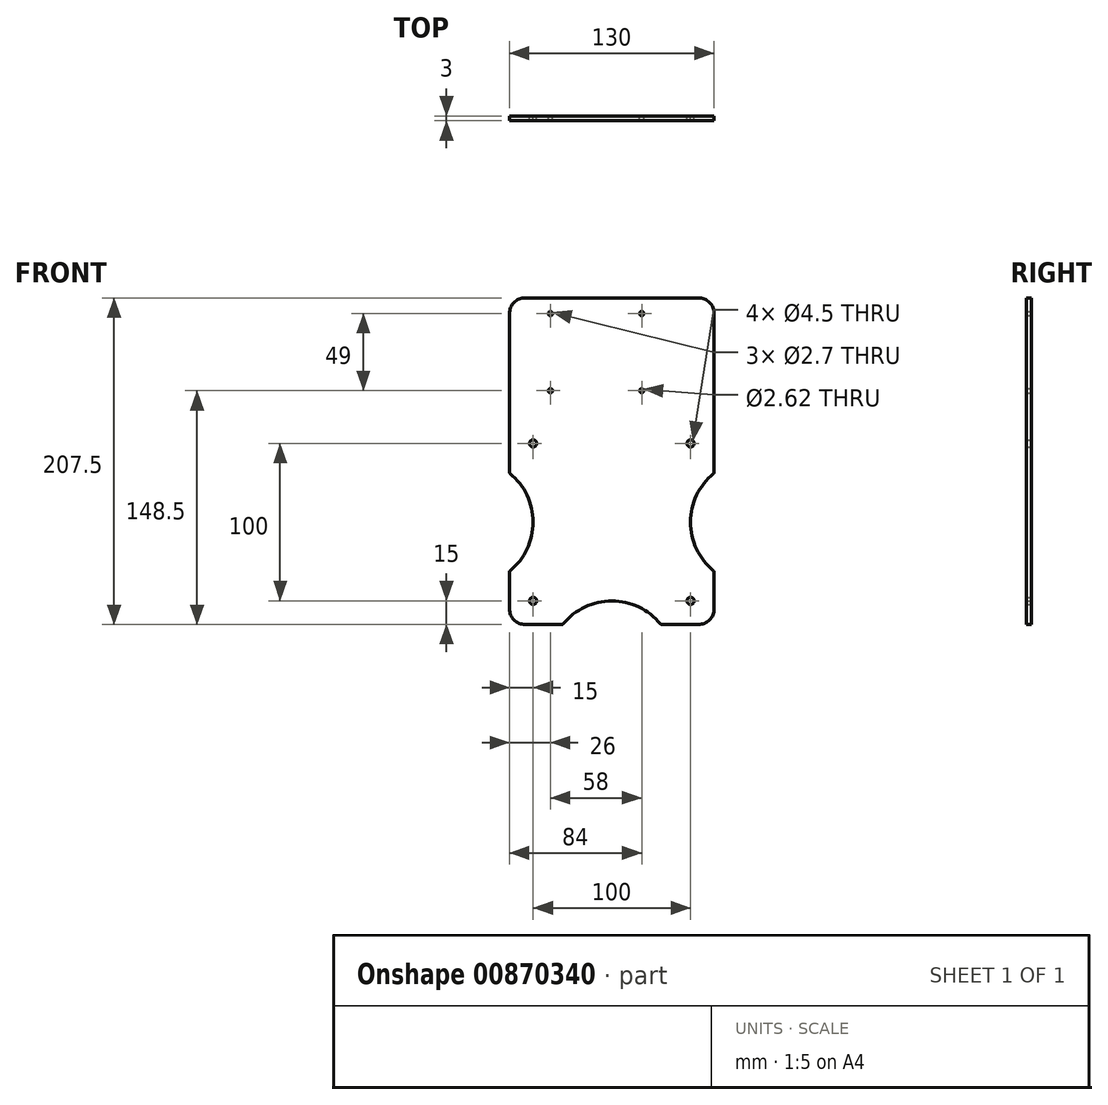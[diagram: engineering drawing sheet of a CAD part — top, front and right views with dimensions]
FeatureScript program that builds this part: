
annotation { "Feature Type Name" : "Feature", "Feature Type Description" : "" }
export const myFeature = defineFeature(function(context is Context, id is Id, definition is map)
    precondition{}
    {
        {
            var Q0;
            Q0=qCreatedBy(makeId("Front.planeOp"),FACE);
            var sketch = newSketch(context, id + "F0", { "sketchPlane" : qUnion([Q0])});
            skLineSegment(sketch, "E0.bottom", {"start": v(10, 0) * mm, "end": v(120, 0) * mm});
            skLineSegment(sketch, "E0.top", {"start": v(10, 207.5) * mm, "end": v(120, 207.5) * mm});
            skLineSegment(sketch, "E0.left", {"start": v(0, 10) * mm, "end": v(0, 197.5) * mm});
            skLineSegment(sketch, "E0.right", {"start": v(130, 10) * mm, "end": v(130, 197.5) * mm});
            skLineSegment(sketch, "E1", {"start": v(65, 0) * mm, "end": v(65, 231.81) * mm, "construction": true});
            skCircle(sketch, "E2", {"center": v(15, 15) * mm, "radius": 2.25 * mm});
            skCircle(sketch, "E3", {"center": v(115, 15) * mm, "radius": 2.25 * mm});
            skCircle(sketch, "E4", {"center": v(15, 115) * mm, "radius": 2.25 * mm});
            skCircle(sketch, "E5", {"center": v(115, 115) * mm, "radius": 2.25 * mm});
            skLineSegment(sketch, "E6.bottom", {"start": v(25.5, 201) * mm, "end": v(104.5, 201) * mm, "construction": true});
            skLineSegment(sketch, "E6.top", {"start": v(25.5, 145) * mm, "end": v(104.5, 145) * mm, "construction": true});
            skLineSegment(sketch, "E6.left", {"start": v(22.5, 198) * mm, "end": v(22.5, 148) * mm, "construction": true});
            skLineSegment(sketch, "E6.right", {"start": v(107.5, 198) * mm, "end": v(107.5, 148) * mm, "construction": true});
            skPoint(sketch, "E7.visualSharp", {"position": v(22.5, 201) * mm});
            skArc(sketch, "E7.filletArc", {"start": v(25.5, 201) * mm, "mid": v(23.38, 200.12) * mm, "end": v(22.5, 198) * mm, "construction": true});
            skPoint(sketch, "E8.visualSharp", {"position": v(107.5, 201) * mm});
            skArc(sketch, "E8.filletArc", {"start": v(107.5, 198) * mm, "mid": v(106.62, 200.12) * mm, "end": v(104.5, 201) * mm, "construction": true});
            skPoint(sketch, "E9.visualSharp", {"position": v(107.5, 145) * mm});
            skArc(sketch, "E9.filletArc", {"start": v(104.5, 145) * mm, "mid": v(106.62, 145.88) * mm, "end": v(107.5, 148) * mm, "construction": true});
            skPoint(sketch, "E10.visualSharp", {"position": v(22.5, 145) * mm});
            skArc(sketch, "E10.filletArc", {"start": v(22.5, 148) * mm, "mid": v(23.38, 145.88) * mm, "end": v(25.5, 145) * mm, "construction": true});
            skCircle(sketch, "E11", {"center": v(26, 197.5) * mm, "radius": 1.35 * mm});
            skCircle(sketch, "E12", {"center": v(26, 148.5) * mm, "radius": 1.35 * mm});
            skCircle(sketch, "E13", {"center": v(84, 148.5) * mm, "radius": 1.31 * mm});
            skCircle(sketch, "E14", {"center": v(84, 197.5) * mm, "radius": 1.35 * mm});
            skPoint(sketch, "E15", {"position": v(65, 201) * mm});
            skPoint(sketch, "E16.visualSharp", {"position": v(0, 207.5) * mm});
            skArc(sketch, "E16.filletArc", {"start": v(10, 207.5) * mm, "mid": v(2.93, 204.57) * mm, "end": v(0, 197.5) * mm});
            skPoint(sketch, "E17.visualSharp", {"position": v(130, 207.5) * mm});
            skArc(sketch, "E17.filletArc", {"start": v(130, 197.5) * mm, "mid": v(127.07, 204.57) * mm, "end": v(120, 207.5) * mm});
            skPoint(sketch, "E18.visualSharp", {"position": v(130, 0) * mm});
            skArc(sketch, "E18.filletArc", {"start": v(120, 0) * mm, "mid": v(127.07, 2.93) * mm, "end": v(130, 10) * mm});
            skPoint(sketch, "E19.visualSharp", {"position": v(0, 0) * mm});
            skArc(sketch, "E19.filletArc", {"start": v(0, 10) * mm, "mid": v(2.93, 2.93) * mm, "end": v(10, 0) * mm});
            skLineSegment(sketch, "E20", {"start": v(0, 65) * mm, "end": v(140.58, 65) * mm, "construction": true});
            skArc(sketch, "E21", {"start": v(0, 33.78) * mm, "mid": v(15, 65) * mm, "end": v(0, 96.22) * mm});
            skArc(sketch, "E22", {"start": v(130, 96.22) * mm, "mid": v(115, 65) * mm, "end": v(130, 33.78) * mm});
            skArc(sketch, "E23", {"start": v(33.78, 0) * mm, "mid": v(65, 15) * mm, "end": v(96.22, 0) * mm});
            skSolve(sketch);
        }
        {
            var Q0;
            Q0=makeQuery(id+"F0.imprint","IMPRINT",FACE,{"disambiguationData":[TD([[makeQuery(id+"F0.imprint","IMPRINT",EDGE,{"derivedFrom":sQuery(id+"F0.wireOp",EDGE,"E0.top")}),-1.0]])]});
            extrude(context, id + "F1", {"entities" : qUnion([Q0]), "depth" : 3 * mm, "offsetDistance" : 25 * mm});
        }
        {
            var Q0;
            {var subQ0=sQuery(id+"F0.wireOp",EDGE,"E21");var subQ1=sQuery(id+"F0.wireOp",EDGE,"E0.left");Q0=makeQuery(id+"F1.opExtrude","SWEPT_EDGE",EDGE,{"disambiguationData":[OSD([subQ1,subQ0]),TDD([makeQuery(id+"F0.imprint","INTERSECT",VERTEX,{"disambiguationData":[OD(0.0)],"derivedFrom":[subQ1,subQ0]})])]});}
            var Q1;
            {var subQ0=sQuery(id+"F0.wireOp",EDGE,"E21");var subQ1=sQuery(id+"F0.wireOp",EDGE,"E0.left");Q1=makeQuery(id+"F1.opExtrude","SWEPT_EDGE",EDGE,{"disambiguationData":[OSD([subQ1,subQ0]),TDD([makeQuery(id+"F0.imprint","INTERSECT",VERTEX,{"disambiguationData":[OD(1.0)],"derivedFrom":[subQ1,subQ0]})])]});}
            var Q2;
            {var subQ0=sQuery(id+"F0.wireOp",EDGE,"E22");var subQ1=sQuery(id+"F0.wireOp",EDGE,"E0.right");Q2=makeQuery(id+"F1.opExtrude","SWEPT_EDGE",EDGE,{"disambiguationData":[OSD([subQ1,subQ0]),TDD([makeQuery(id+"F0.imprint","INTERSECT",VERTEX,{"disambiguationData":[OD(0.0)],"derivedFrom":[subQ1,subQ0]})])]});}
            var Q3;
            {var subQ0=sQuery(id+"F0.wireOp",EDGE,"E22");var subQ1=sQuery(id+"F0.wireOp",EDGE,"E0.right");Q3=makeQuery(id+"F1.opExtrude","SWEPT_EDGE",EDGE,{"disambiguationData":[OSD([subQ1,subQ0]),TDD([makeQuery(id+"F0.imprint","INTERSECT",VERTEX,{"disambiguationData":[OD(1.0)],"derivedFrom":[subQ1,subQ0]})])]});}
            var Q4;
            {var subQ0=sQuery(id+"F0.wireOp",EDGE,"E23");var subQ1=sQuery(id+"F0.wireOp",EDGE,"E0.bottom");Q4=makeQuery(id+"F1.opExtrude","SWEPT_EDGE",EDGE,{"disambiguationData":[OSD([subQ1,subQ0]),TDD([makeQuery(id+"F0.imprint","INTERSECT",VERTEX,{"disambiguationData":[OD(1.0)],"derivedFrom":[subQ1,subQ0]})])]});}
            var Q5;
            {var subQ0=sQuery(id+"F0.wireOp",EDGE,"E23");var subQ1=sQuery(id+"F0.wireOp",EDGE,"E0.bottom");Q5=makeQuery(id+"F1.opExtrude","SWEPT_EDGE",EDGE,{"disambiguationData":[OSD([subQ1,subQ0]),TDD([makeQuery(id+"F0.imprint","INTERSECT",VERTEX,{"disambiguationData":[OD(0.0)],"derivedFrom":[subQ1,subQ0]})])]});}
            fillet(context, id + "F2", {"entities" : qUnion([Q0, Q1, Q2, Q3, Q4, Q5]), "radius" : 1 * mm, "tangentPropagation" : true, "allowEdgeOverflow" : false});
        }
    });
